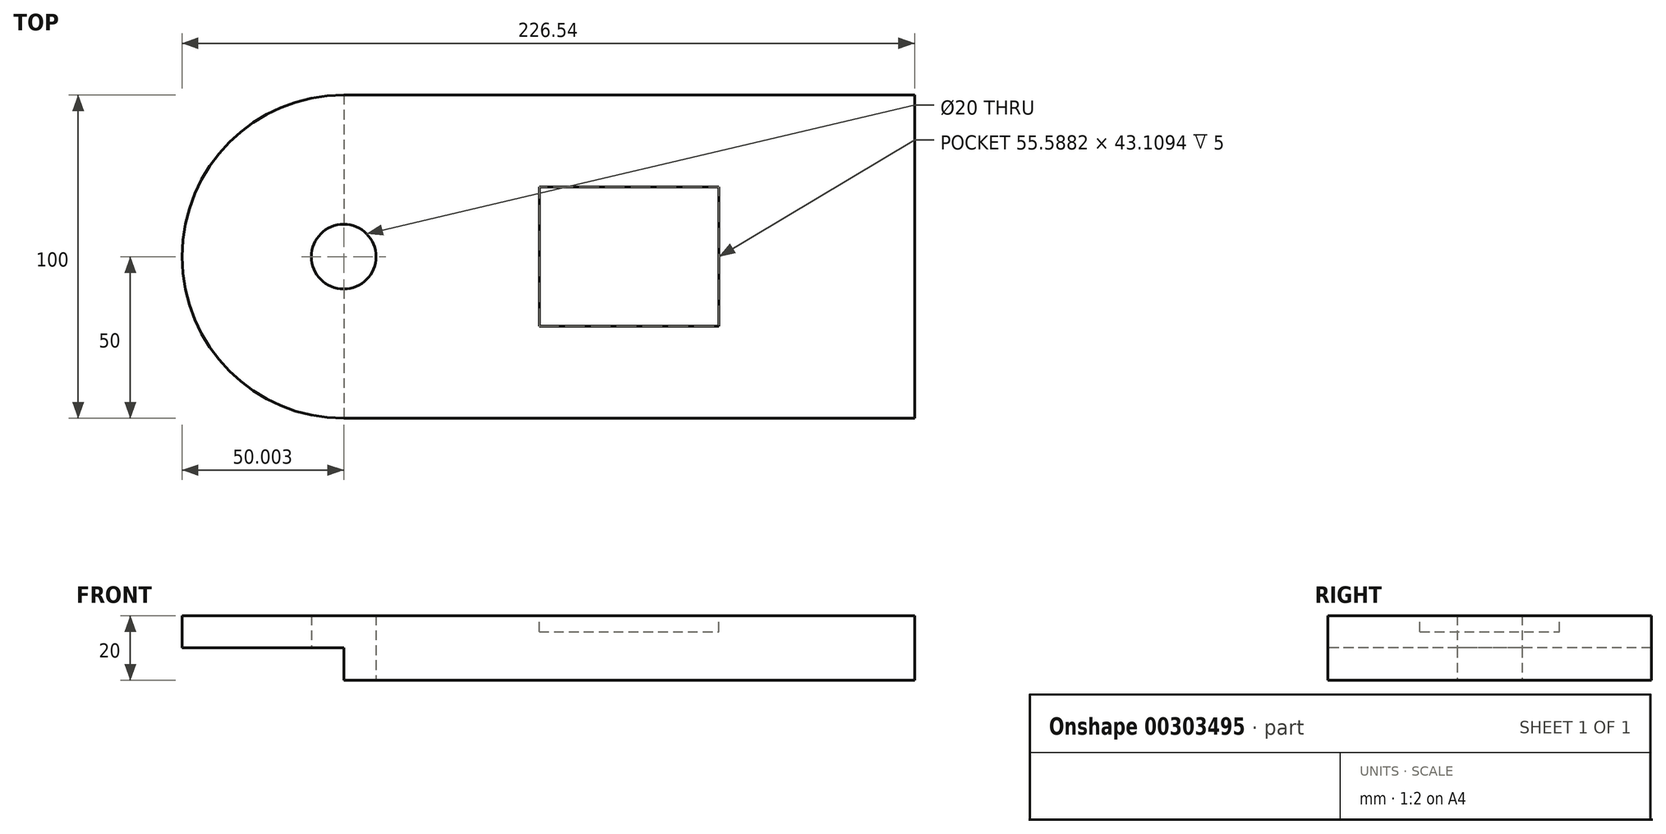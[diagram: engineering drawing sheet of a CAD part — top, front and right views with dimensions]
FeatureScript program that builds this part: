
annotation { "Feature Type Name" : "Feature", "Feature Type Description" : "" }
export const myFeature = defineFeature(function(context is Context, id is Id, definition is map)
    precondition{}
    {
        {
            var Q0;
            Q0=qCreatedBy(makeId("Top.planeOp"),FACE);
            var sketch = newSketch(context, id + "F0", { "sketchPlane" : qUnion([Q0])});
            skLineSegment(sketch, "E0.bottom", {"start": v(-88.27, 50) * mm, "end": v(88.27, 50) * mm});
            skLineSegment(sketch, "E0.top", {"start": v(-88.27, -50) * mm, "end": v(88.27, -50) * mm});
            skLineSegment(sketch, "E0.left", {"start": v(-88.27, 50) * mm, "end": v(-88.27, -50) * mm});
            skLineSegment(sketch, "E0.right", {"start": v(88.27, 50) * mm, "end": v(88.27, -50) * mm});
            skPoint(sketch, "E0.middle", {"position": v(0, 0) * mm});
            skCircle(sketch, "E1", {"center": v(-88.27, 0) * mm, "radius": 50 * mm});
            skCircle(sketch, "E2", {"center": v(-88.27, 0) * mm, "radius": 10 * mm});
            skSolve(sketch);
        }
        {
            var Q0;
            Q0 = qSketchRegion(id + "F0", true);
            extrude(context, id + "F1", {"entities" : qUnion([Q0]), "depth" : 20 * mm});
        }
        {
            var Q0;
            {var subQ1=sQuery(id+"F0.wireOp",EDGE,"E0.left");var subQ3=sQuery(id+"F0.wireOp",EDGE,"E2");var subQ4=makeQuery(id+"F0.imprint","INTERSECT",VERTEX,{"disambiguationData":[OD(0.0)],"derivedFrom":[subQ1,subQ3]});Q0=makeQuery(id+"F0.imprint","IMPRINT",FACE,{"disambiguationData":[TD([[makeQuery(id+"F0.imprint","IMPRINT",EDGE,{"disambiguationData":[TD([[subQ4,-1.0]])],"derivedFrom":subQ3}),-1.0]])]});}
            extrude(context, id + "F2", {"entities" : qUnion([Q0]), "operationType" : NewBodyOperationType.REMOVE, "depth" : 10 * mm});
        }
        {
            var Q0;
            Q0=makeQuery(id+"F1.opExtrude","CAP_FACE",FACE,{"disambiguationData":[OSD([sQuery(id+"F0.wireOp",EDGE,"E0.bottom"),sQuery(id+"F0.wireOp",EDGE,"E0.top"),sQuery(id+"F0.wireOp",EDGE,"E0.right"),sQuery(id+"F0.wireOp",EDGE,"E1"),sQuery(id+"F0.wireOp",EDGE,"E2")])],"isStart":false});
            var sketch = newSketch(context, id + "F3", { "sketchPlane" : qUnion([Q0])});
            skLineSegment(sketch, "E3.bottom", {"start": v(-27.8, -21.55) * mm, "end": v(27.8, -21.55) * mm});
            skLineSegment(sketch, "E3.top", {"start": v(-27.8, 21.55) * mm, "end": v(27.8, 21.55) * mm});
            skLineSegment(sketch, "E3.left", {"start": v(-27.8, -21.55) * mm, "end": v(-27.8, 21.55) * mm});
            skLineSegment(sketch, "E3.right", {"start": v(27.8, -21.55) * mm, "end": v(27.8, 21.55) * mm});
            skPoint(sketch, "E3.middle", {"position": v(0, 0) * mm});
            skSolve(sketch);
        }
        {
            var Q0;
            Q0=makeQuery(id+"F3.imprint","IMPRINT",FACE,{"disambiguationData":[TD([[makeQuery(id+"F3.imprint","IMPRINT",EDGE,{"derivedFrom":sQuery(id+"F3.wireOp",EDGE,"E3.bottom")}),1.0]])]});
            extrude(context, id + "F4", {"entities" : qUnion([Q0]), "operationType" : NewBodyOperationType.REMOVE, "oppositeDirection" : true, "depth" : 5 * mm});
        }
    });
